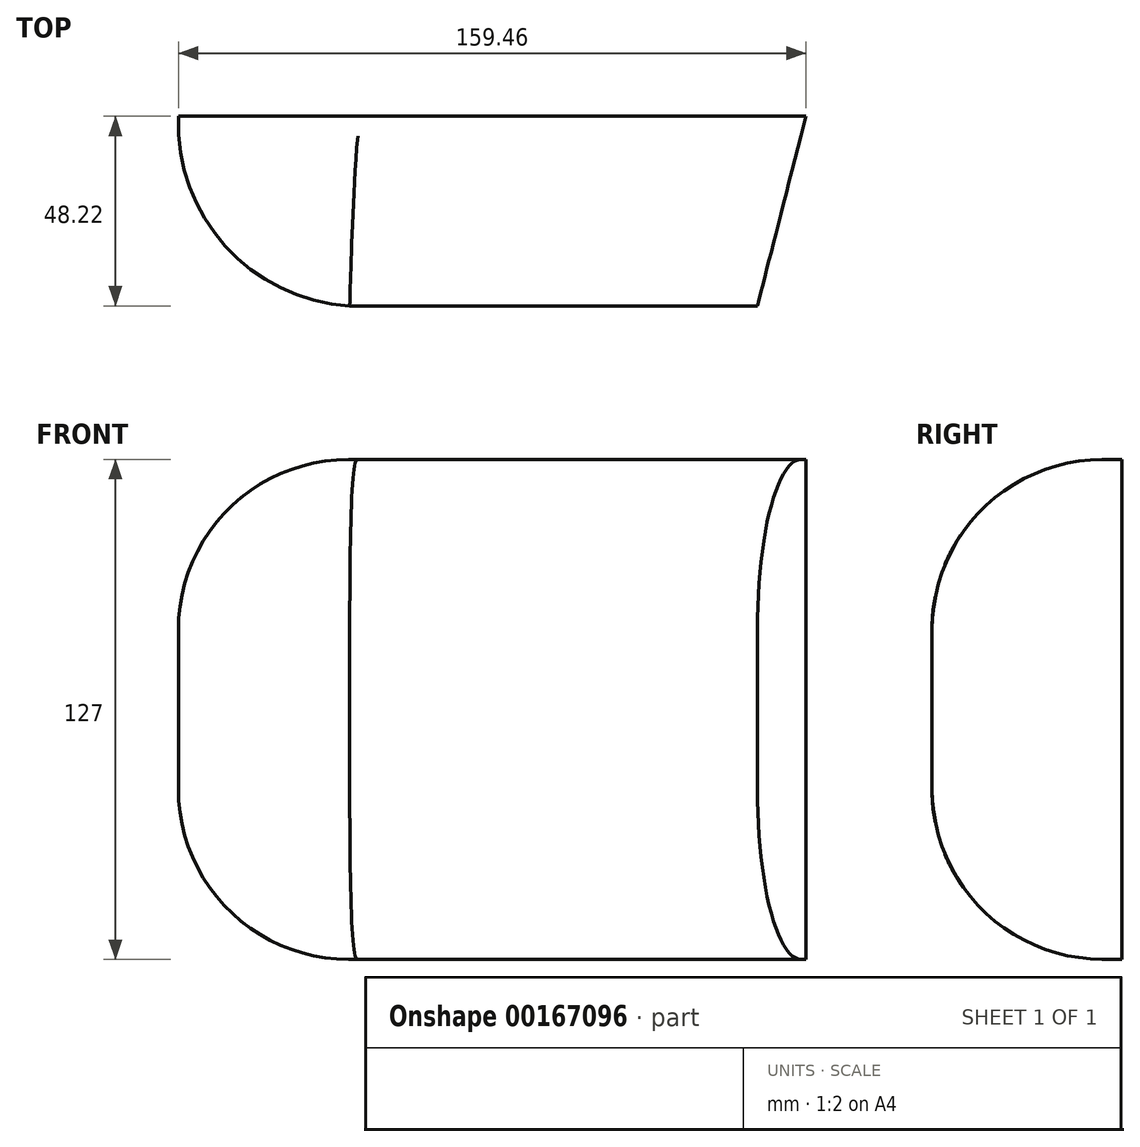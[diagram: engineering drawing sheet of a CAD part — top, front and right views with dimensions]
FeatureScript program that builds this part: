
annotation { "Feature Type Name" : "Feature", "Feature Type Description" : "" }
export const myFeature = defineFeature(function(context is Context, id is Id, definition is map)
    precondition{}
    {
        {
            var Q0;
            Q0=qCreatedBy(makeId("Top.planeOp"),FACE);
            var sketch = newSketch(context, id + "F0", { "sketchPlane" : qUnion([Q0])});
            skLineSegment(sketch, "E0", {"start": v(54.77, 12.92) * mm, "end": v(67.15, 61.14) * mm});
            skLineSegment(sketch, "E1", {"start": v(67.15, 61.14) * mm, "end": v(-92.26, 61.14) * mm});
            skLineSegment(sketch, "E2", {"start": v(54.77, 12.92) * mm, "end": v(4.6, 12.92) * mm});
            skArc(sketch, "E3", {"start": v(-92.26, 61.14) * mm, "mid": v(-80.39, 28.14) * mm, "end": v(-48.8, 12.92) * mm});
            skLineSegment(sketch, "E4", {"start": v(-48.8, 12.92) * mm, "end": v(4.6, 12.92) * mm});
            skSolve(sketch);
        }
        {
            var Q0;
            Q0 = qSketchRegion(id + "F0", true);
            extrude(context, id + "F1", {"entities" : qUnion([Q0]), "depth" : 127 * mm});
        }
        {
            var Q0;
            Q0=makeQuery(id+"F1.opExtrude","CAP_EDGE",EDGE,{"disambiguationData":[OSD([sQuery(id+"F0.wireOp",EDGE,"E2"),sQuery(id+"F0.wireOp",EDGE,"E4")])],"isStart":false});
            var Q1;
            Q1=makeQuery(id+"F1.opExtrude","CAP_EDGE",EDGE,{"disambiguationData":[OSD([sQuery(id+"F0.wireOp",EDGE,"E3")])],"isStart":false});
            fillet(context, id + "F2", {"entities" : qUnion([Q0, Q1]), "radius" : 43.18 * mm, "tangentPropagation" : true, "allowEdgeOverflow" : false});
        }
        {
            var Q0;
            Q0=makeQuery(id+"F1.opExtrude","CAP_EDGE",EDGE,{"disambiguationData":[OSD([sQuery(id+"F0.wireOp",EDGE,"E2"),sQuery(id+"F0.wireOp",EDGE,"E4")])],"isStart":true});
            var Q1;
            Q1=makeQuery(id+"F1.opExtrude","CAP_EDGE",EDGE,{"disambiguationData":[OSD([sQuery(id+"F0.wireOp",EDGE,"E3")])],"isStart":true});
            fillet(context, id + "F3", {"entities" : qUnion([Q0, Q1]), "radius" : 43.18 * mm, "tangentPropagation" : true, "allowEdgeOverflow" : false});
        }
    });
